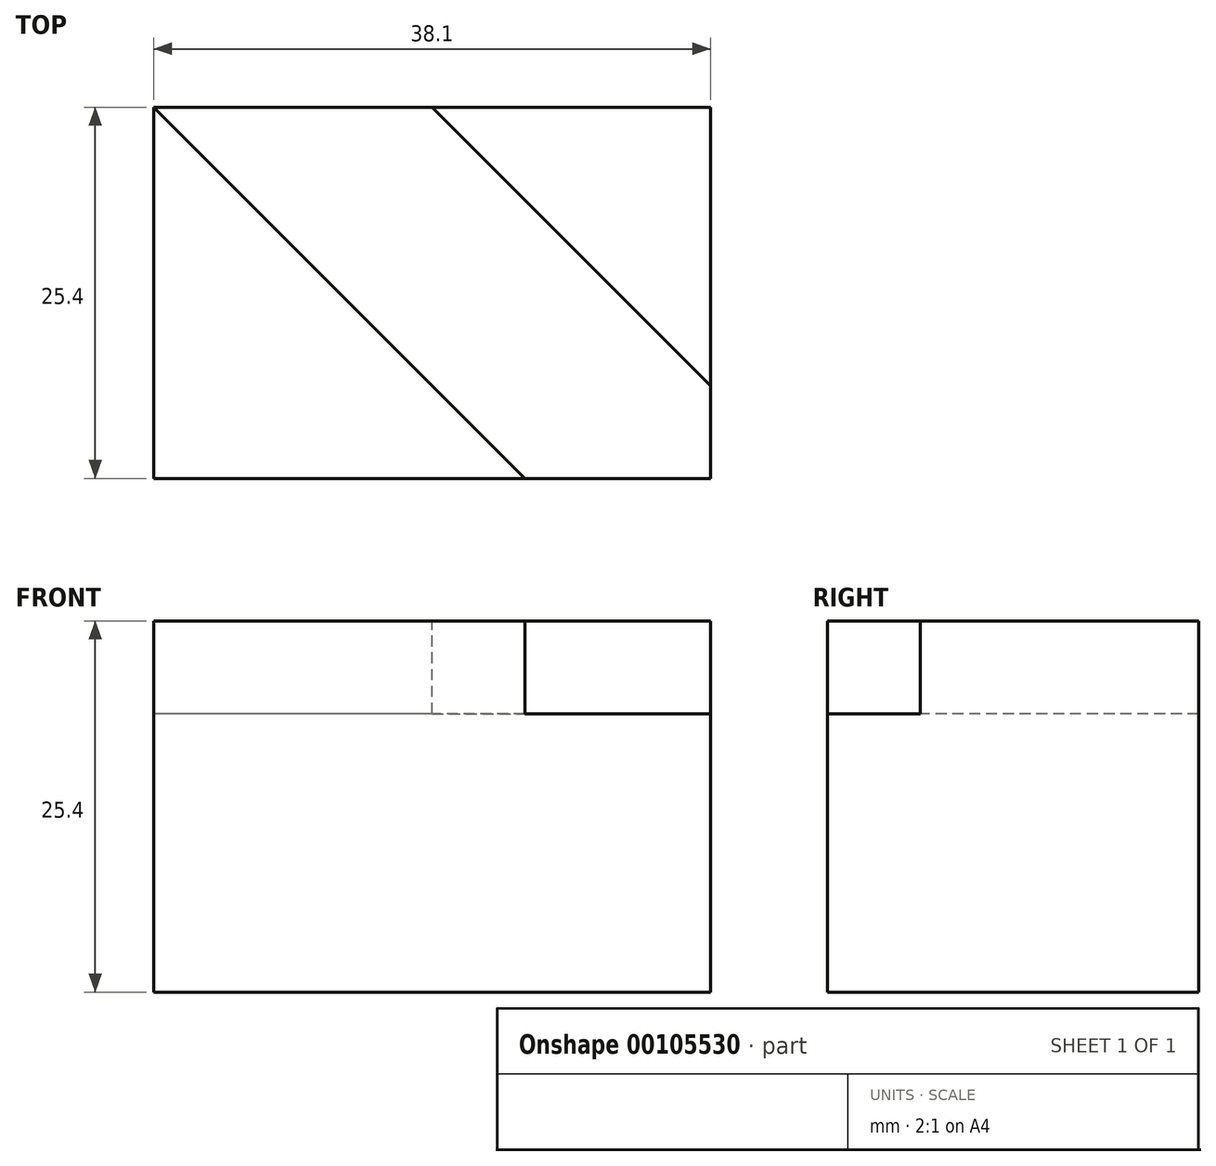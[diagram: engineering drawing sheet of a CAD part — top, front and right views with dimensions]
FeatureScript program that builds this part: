
annotation { "Feature Type Name" : "Feature", "Feature Type Description" : "" }
export const myFeature = defineFeature(function(context is Context, id is Id, definition is map)
    precondition{}
    {
        {
            var Q0;
            Q0=qCreatedBy(makeId("Right.planeOp"),FACE);
            var sketch = newSketch(context, id + "F0", { "sketchPlane" : qUnion([Q0])});
            skLineSegment(sketch, "E0", {"start": v(0, 0) * mm, "end": v(0, 25.4) * mm});
            skLineSegment(sketch, "E1", {"start": v(0, 25.4) * mm, "end": v(-25.4, 25.4) * mm});
            skLineSegment(sketch, "E2", {"start": v(-25.4, 25.4) * mm, "end": v(-25.4, 0) * mm});
            skLineSegment(sketch, "E3", {"start": v(-25.4, 0) * mm, "end": v(0, 0) * mm});
            skSolve(sketch);
        }
        {
            var Q0;
            Q0=makeQuery(id+"F0.imprint","IMPRINT",FACE,{"disambiguationData":[TD([[makeQuery(id+"F0.imprint","IMPRINT",EDGE,{"derivedFrom":sQuery(id+"F0.wireOp",EDGE,"E0")}),1.0]])]});
            extrude(context, id + "F1", {"entities" : qUnion([Q0]), "depth" : 38.1 * mm});
        }
        {
            var Q0;
            Q0=makeQuery(id+"F1.opExtrude","SWEPT_FACE",FACE,{"disambiguationData":[OSD([sQuery(id+"F0.wireOp",EDGE,"E1")])]});
            var sketch = newSketch(context, id + "F2", { "sketchPlane" : qUnion([Q0])});
            skLineSegment(sketch, "E4", {"start": v(0, 0) * mm, "end": v(19.05, 0) * mm});
            skLineSegment(sketch, "E5", {"start": v(19.05, 0) * mm, "end": v(38.1, -19.05) * mm});
            skLineSegment(sketch, "E6", {"start": v(38.1, -19.05) * mm, "end": v(38.1, -25.4) * mm});
            skLineSegment(sketch, "E7", {"start": v(38.1, -25.4) * mm, "end": v(25.4, -25.4) * mm});
            skLineSegment(sketch, "E8", {"start": v(25.4, -25.4) * mm, "end": v(0, 0) * mm});
            skSolve(sketch);
        }
        {
            var Q0;
            Q0 = qSketchRegion(id + "F2", true);
            extrude(context, id + "F3", {"entities" : qUnion([Q0]), "operationType" : NewBodyOperationType.REMOVE, "oppositeDirection" : true, "depth" : 6.35 * mm});
        }
    });
